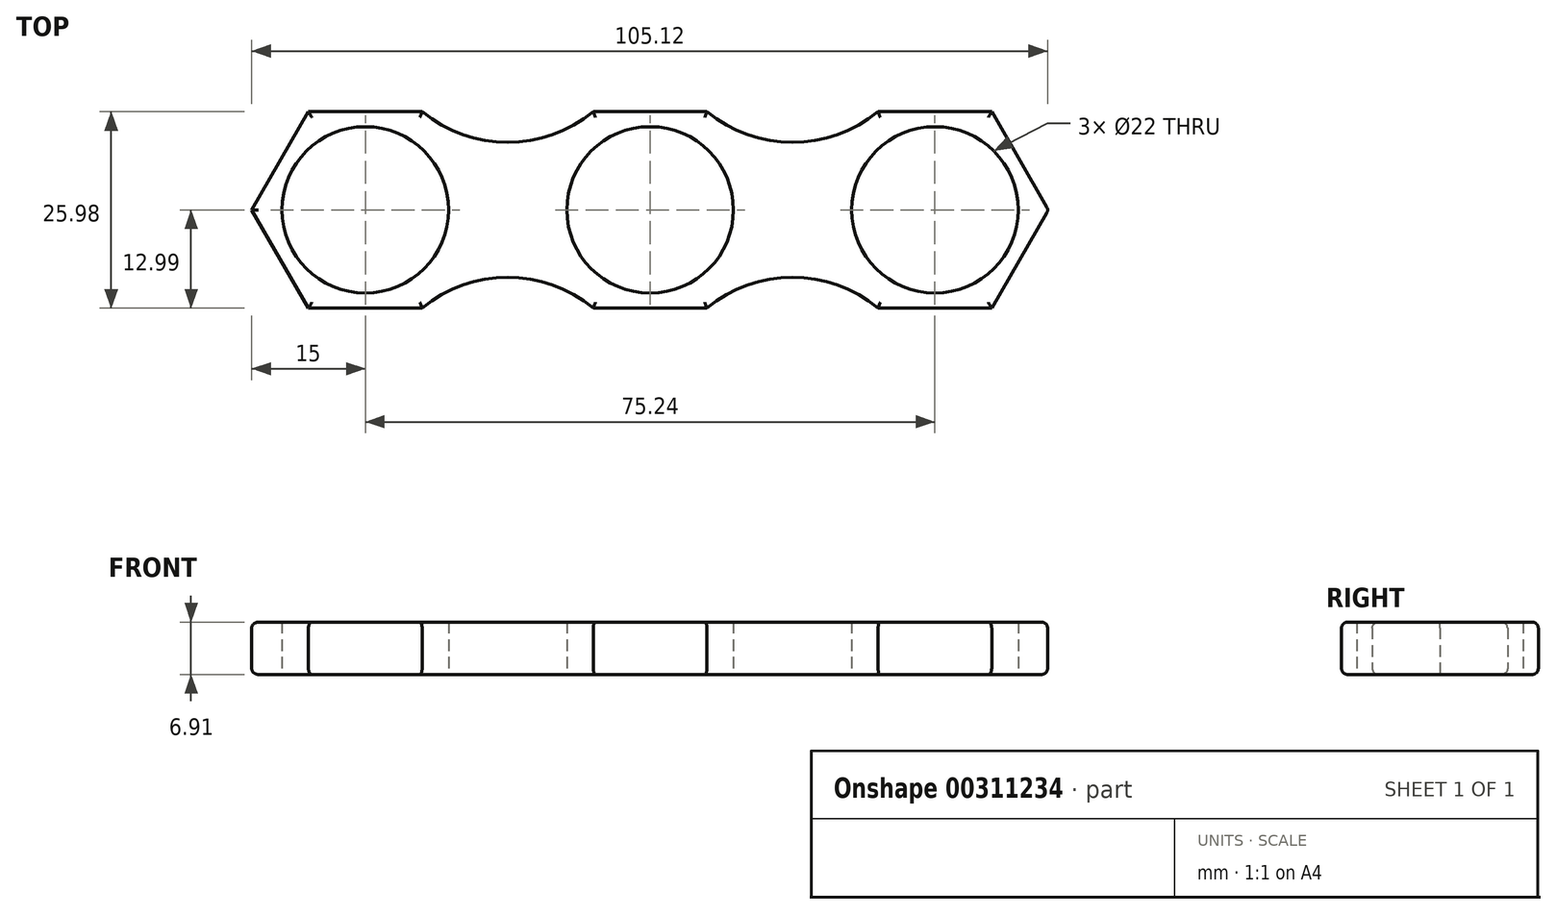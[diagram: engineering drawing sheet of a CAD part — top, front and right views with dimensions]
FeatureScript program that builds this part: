
annotation { "Feature Type Name" : "Feature", "Feature Type Description" : "" }
export const myFeature = defineFeature(function(context is Context, id is Id, definition is map)
    precondition{}
    {
        {
            var Q0;
            Q0=qCreatedBy(makeId("Top.planeOp"),FACE);
            var sketch = newSketch(context, id + "F0", { "sketchPlane" : qUnion([Q0])});
            skCircle(sketch, "E0.cCircle", {"center": v(0, 0) * mm, "radius": 15 * mm, "construction": true});
            skLineSegment(sketch, "E0.0", {"start": v(15, 0) * mm, "end": v(7.5, -13) * mm});
            skLineSegment(sketch, "E0.1", {"start": v(7.5, -13) * mm, "end": v(-7.5, -13) * mm});
            skLineSegment(sketch, "E0.2", {"start": v(-7.5, -13) * mm, "end": v(-15, 0) * mm});
            skLineSegment(sketch, "E0.3", {"start": v(-15, 0) * mm, "end": v(-7.5, 13) * mm});
            skLineSegment(sketch, "E0.4", {"start": v(-7.5, 13) * mm, "end": v(7.5, 13) * mm});
            skLineSegment(sketch, "E0.5", {"start": v(7.5, 13) * mm, "end": v(15, 0) * mm});
            skCircle(sketch, "E1.cCircle", {"center": v(37.62, 0) * mm, "radius": 15 * mm, "construction": true});
            skLineSegment(sketch, "E1.0", {"start": v(52.62, 0) * mm, "end": v(45.12, -13) * mm});
            skLineSegment(sketch, "E1.1", {"start": v(45.12, -13) * mm, "end": v(30.12, -13) * mm});
            skLineSegment(sketch, "E1.2", {"start": v(30.12, -13) * mm, "end": v(22.62, 0) * mm});
            skLineSegment(sketch, "E1.3", {"start": v(22.62, 0) * mm, "end": v(30.12, 13) * mm});
            skLineSegment(sketch, "E1.4", {"start": v(30.12, 13) * mm, "end": v(45.12, 13) * mm});
            skLineSegment(sketch, "E1.5", {"start": v(45.12, 13) * mm, "end": v(52.62, 0) * mm});
            skCircle(sketch, "E2.cCircle", {"center": v(-37.62, 0) * mm, "radius": 15 * mm, "construction": true});
            skLineSegment(sketch, "E2.0", {"start": v(-22.62, 0) * mm, "end": v(-30.12, -13) * mm});
            skLineSegment(sketch, "E2.1", {"start": v(-30.12, -13) * mm, "end": v(-45.12, -13) * mm});
            skLineSegment(sketch, "E2.2", {"start": v(-45.12, -13) * mm, "end": v(-52.62, 0) * mm});
            skLineSegment(sketch, "E2.3", {"start": v(-52.62, 0) * mm, "end": v(-45.12, 13) * mm});
            skLineSegment(sketch, "E2.4", {"start": v(-45.12, 13) * mm, "end": v(-30.12, 13) * mm});
            skLineSegment(sketch, "E2.5", {"start": v(-30.12, 13) * mm, "end": v(-22.62, 0) * mm});
            skLineSegment(sketch, "E3", {"start": v(7.5, 13) * mm, "end": v(30.12, 13) * mm});
            skLineSegment(sketch, "E4", {"start": v(7.5, -13) * mm, "end": v(30.12, -13) * mm});
            skLineSegment(sketch, "E5", {"start": v(-7.5, -13) * mm, "end": v(-30.12, -13) * mm});
            skLineSegment(sketch, "E6", {"start": v(-7.5, 13) * mm, "end": v(-30.12, 13) * mm});
            skCircle(sketch, "E7", {"center": v(-37.62, 0) * mm, "radius": 11 * mm});
            skCircle(sketch, "E8", {"center": v(0, 0) * mm, "radius": 11 * mm});
            skCircle(sketch, "E9", {"center": v(37.62, 0) * mm, "radius": 11 * mm});
            skLineSegment(sketch, "E10", {"start": v(-73.02, 0) * mm, "end": v(75.13, 0) * mm, "construction": true});
            skArc(sketch, "E11", {"start": v(-30.12, 13) * mm, "mid": v(-18.8, 8.93) * mm, "end": v(-7.5, 13) * mm});
            skArc(sketch, "E12", {"start": v(7.5, 13) * mm, "mid": v(18.8, 8.93) * mm, "end": v(30.12, 13) * mm});
            skArc(sketch, "E13", {"start": v(-7.5, -13) * mm, "mid": v(-18.8, -8.93) * mm, "end": v(-30.12, -13) * mm});
            skArc(sketch, "E14", {"start": v(30.12, -13) * mm, "mid": v(18.81, -8.93) * mm, "end": v(7.5, -13) * mm});
            skSolve(sketch);
        }
        {
            var Q0;
            Q0=makeQuery(id+"F0.imprint","IMPRINT",FACE,{"disambiguationData":[TD([[makeQuery(id+"F0.imprint","IMPRINT",EDGE,{"derivedFrom":sQuery(id+"F0.wireOp",EDGE,"E0.2")}),1.0]])]});
            var Q1;
            Q1=makeQuery(id+"F0.imprint","IMPRINT",FACE,{"disambiguationData":[TD([[makeQuery(id+"F0.imprint","IMPRINT",EDGE,{"derivedFrom":sQuery(id+"F0.wireOp",EDGE,"E1.0")}),-1.0]])]});
            var Q2;
            Q2=makeQuery(id+"F0.imprint","IMPRINT",FACE,{"disambiguationData":[TD([[makeQuery(id+"F0.imprint","IMPRINT",EDGE,{"derivedFrom":sQuery(id+"F0.wireOp",EDGE,"E2.0")}),-1.0]])]});
            var Q3;
            Q3=makeQuery(id+"F0.imprint","IMPRINT",FACE,{"disambiguationData":[TD([[makeQuery(id+"F0.imprint","IMPRINT",EDGE,{"derivedFrom":sQuery(id+"F0.wireOp",EDGE,"E0.0")}),-1.0]])]});
            var Q4;
            Q4=makeQuery(id+"F0.imprint","IMPRINT",FACE,{"disambiguationData":[TD([[makeQuery(id+"F0.imprint","IMPRINT",EDGE,{"derivedFrom":sQuery(id+"F0.wireOp",EDGE,"E0.0")}),1.0]])]});
            extrude(context, id + "F1", {"entities" : qUnion([Q0, Q1, Q2, Q3, Q4]), "depth" : 6.9 * mm});
        }
        {
            var Q0;
            Q0=makeQuery(id+"F1.opExtrude","CAP_EDGE",EDGE,{"disambiguationData":[OSD([sQuery(id+"F0.wireOp",EDGE,"E2.4")])],"isStart":false});
            var Q1;
            Q1=makeQuery(id+"F1.opExtrude","CAP_EDGE",EDGE,{"disambiguationData":[OSD([sQuery(id+"F0.wireOp",EDGE,"E11")])],"isStart":false});
            var Q2;
            Q2=makeQuery(id+"F1.opExtrude","CAP_EDGE",EDGE,{"disambiguationData":[OSD([sQuery(id+"F0.wireOp",EDGE,"E0.4")])],"isStart":false});
            var Q3;
            Q3=makeQuery(id+"F1.opExtrude","CAP_EDGE",EDGE,{"disambiguationData":[OSD([sQuery(id+"F0.wireOp",EDGE,"E12")])],"isStart":false});
            var Q4;
            Q4=makeQuery(id+"F1.opExtrude","CAP_EDGE",EDGE,{"disambiguationData":[OSD([sQuery(id+"F0.wireOp",EDGE,"E1.5")])],"isStart":false});
            var Q5;
            Q5=makeQuery(id+"F1.opExtrude","CAP_EDGE",EDGE,{"disambiguationData":[OSD([sQuery(id+"F0.wireOp",EDGE,"E1.0")])],"isStart":false});
            var Q6;
            Q6=makeQuery(id+"F1.opExtrude","CAP_EDGE",EDGE,{"disambiguationData":[OSD([sQuery(id+"F0.wireOp",EDGE,"E1.1")])],"isStart":false});
            var Q7;
            Q7=makeQuery(id+"F1.opExtrude","CAP_EDGE",EDGE,{"disambiguationData":[OSD([sQuery(id+"F0.wireOp",EDGE,"E14")])],"isStart":false});
            var Q8;
            Q8=makeQuery(id+"F1.opExtrude","CAP_EDGE",EDGE,{"disambiguationData":[OSD([sQuery(id+"F0.wireOp",EDGE,"E0.1")])],"isStart":false});
            var Q9;
            Q9=makeQuery(id+"F1.opExtrude","CAP_EDGE",EDGE,{"disambiguationData":[OSD([sQuery(id+"F0.wireOp",EDGE,"E2.1")])],"isStart":false});
            var Q10;
            Q10=makeQuery(id+"F1.opExtrude","CAP_EDGE",EDGE,{"disambiguationData":[OSD([sQuery(id+"F0.wireOp",EDGE,"E2.3")])],"isStart":false});
            var Q11;
            Q11=makeQuery(id+"F1.opExtrude","CAP_EDGE",EDGE,{"disambiguationData":[OSD([sQuery(id+"F0.wireOp",EDGE,"E2.2")])],"isStart":false});
            var Q12;
            Q12=makeQuery(id+"F1.opExtrude","CAP_EDGE",EDGE,{"disambiguationData":[OSD([sQuery(id+"F0.wireOp",EDGE,"E13")])],"isStart":false});
            var Q13;
            Q13=makeQuery(id+"F1.opExtrude","CAP_EDGE",EDGE,{"disambiguationData":[OSD([sQuery(id+"F0.wireOp",EDGE,"E1.4")])],"isStart":false});
            var Q14;
            Q14=makeQuery(id+"F1.opExtrude","CAP_EDGE",EDGE,{"disambiguationData":[OSD([sQuery(id+"F0.wireOp",EDGE,"E14")])],"isStart":true});
            var Q15;
            Q15=makeQuery(id+"F1.opExtrude","CAP_EDGE",EDGE,{"disambiguationData":[OSD([sQuery(id+"F0.wireOp",EDGE,"E0.1")])],"isStart":true});
            var Q16;
            Q16=makeQuery(id+"F1.opExtrude","CAP_EDGE",EDGE,{"disambiguationData":[OSD([sQuery(id+"F0.wireOp",EDGE,"E13")])],"isStart":true});
            var Q17;
            Q17=makeQuery(id+"F1.opExtrude","CAP_EDGE",EDGE,{"disambiguationData":[OSD([sQuery(id+"F0.wireOp",EDGE,"E2.1")])],"isStart":true});
            var Q18;
            Q18=makeQuery(id+"F1.opExtrude","CAP_EDGE",EDGE,{"disambiguationData":[OSD([sQuery(id+"F0.wireOp",EDGE,"E2.2")])],"isStart":true});
            var Q19;
            Q19=makeQuery(id+"F1.opExtrude","CAP_EDGE",EDGE,{"disambiguationData":[OSD([sQuery(id+"F0.wireOp",EDGE,"E2.3")])],"isStart":true});
            var Q20;
            Q20=makeQuery(id+"F1.opExtrude","CAP_EDGE",EDGE,{"disambiguationData":[OSD([sQuery(id+"F0.wireOp",EDGE,"E1.1")])],"isStart":true});
            var Q21;
            Q21=makeQuery(id+"F1.opExtrude","CAP_EDGE",EDGE,{"disambiguationData":[OSD([sQuery(id+"F0.wireOp",EDGE,"E1.0")])],"isStart":true});
            var Q22;
            Q22=makeQuery(id+"F1.opExtrude","SWEPT_EDGE",EDGE,{"disambiguationData":[OSD([sQuery(id+"F0.wireOp",EDGE,"E1.0"),sQuery(id+"F0.wireOp",EDGE,"E1.5")])]});
            var Q23;
            Q23=makeQuery(id+"F1.opExtrude","CAP_EDGE",EDGE,{"disambiguationData":[OSD([sQuery(id+"F0.wireOp",EDGE,"E1.4")])],"isStart":true});
            var Q24;
            Q24=makeQuery(id+"F1.opExtrude","CAP_EDGE",EDGE,{"disambiguationData":[OSD([sQuery(id+"F0.wireOp",EDGE,"E12")])],"isStart":true});
            var Q25;
            Q25=makeQuery(id+"F1.opExtrude","CAP_EDGE",EDGE,{"disambiguationData":[OSD([sQuery(id+"F0.wireOp",EDGE,"E0.4")])],"isStart":true});
            var Q26;
            Q26=makeQuery(id+"F1.opExtrude","CAP_EDGE",EDGE,{"disambiguationData":[OSD([sQuery(id+"F0.wireOp",EDGE,"E11")])],"isStart":true});
            var Q27;
            Q27=makeQuery(id+"F1.opExtrude","CAP_EDGE",EDGE,{"disambiguationData":[OSD([sQuery(id+"F0.wireOp",EDGE,"E2.4")])],"isStart":true});
            var Q28;
            Q28=makeQuery(id+"F1.opExtrude","CAP_EDGE",EDGE,{"disambiguationData":[OSD([sQuery(id+"F0.wireOp",EDGE,"E1.5")])],"isStart":true});
            fillet(context, id + "F2", {"entities" : qUnion([Q0, Q1, Q2, Q3, Q4, Q5, Q6, Q7, Q8, Q9, Q10, Q11, Q12, Q13, Q14, Q15, Q16, Q17, Q18, Q19, Q20, Q21, Q22, Q23, Q24, Q25, Q26, Q27, Q28]), "radius" : 0.76 * mm, "tangentPropagation" : true, "allowEdgeOverflow" : false});
        }
    });
